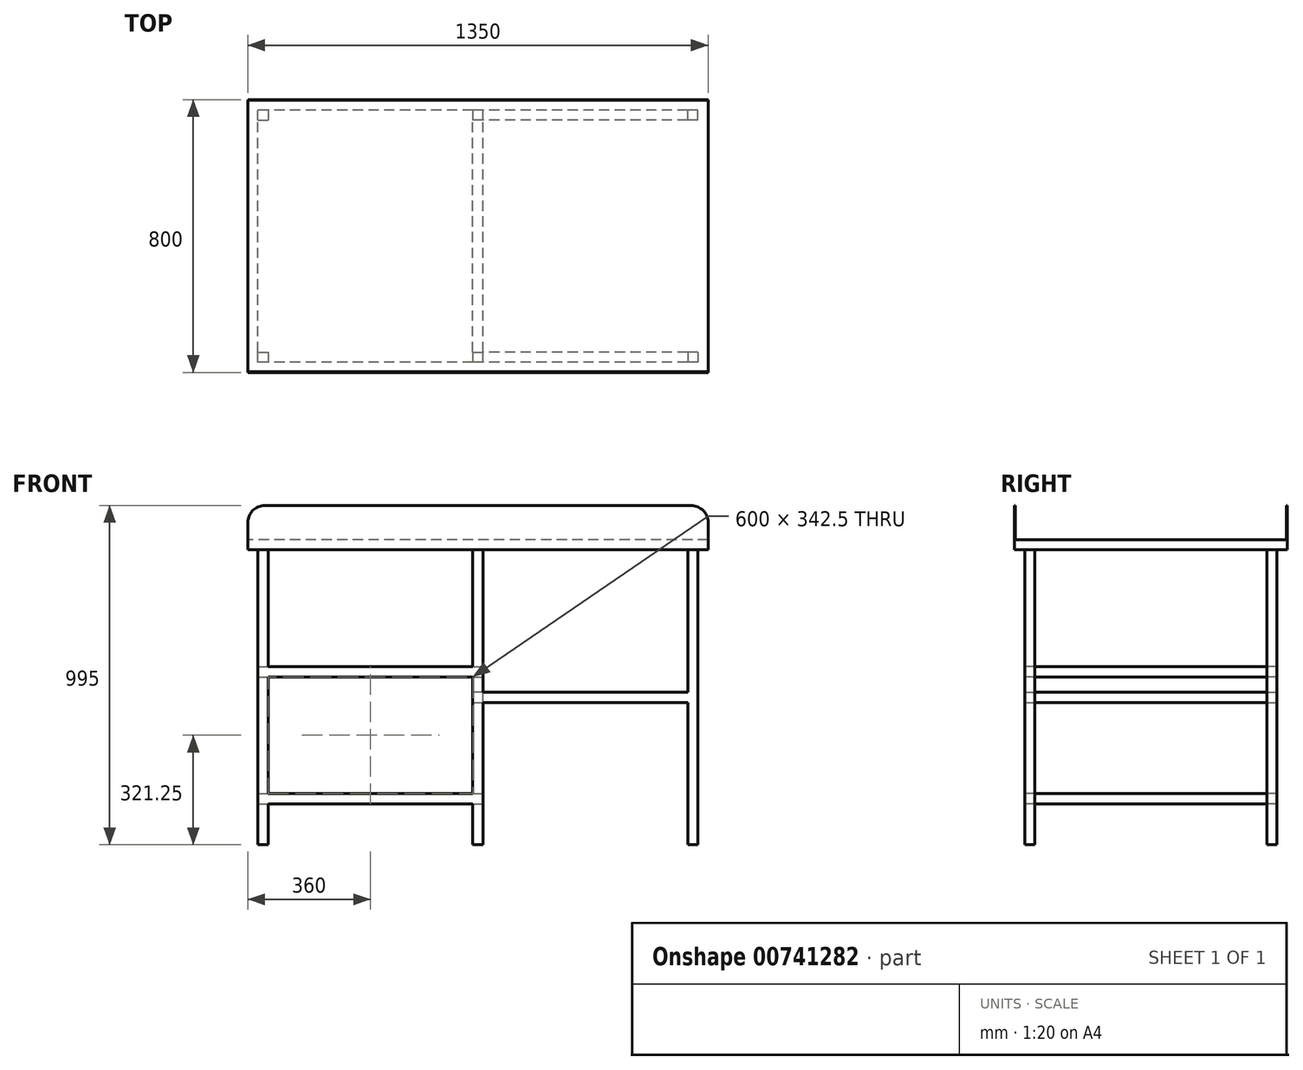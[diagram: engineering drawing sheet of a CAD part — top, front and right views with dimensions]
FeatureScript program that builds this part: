
annotation { "Feature Type Name" : "Feature", "Feature Type Description" : "" }
export const myFeature = defineFeature(function(context is Context, id is Id, definition is map)
    precondition{}
    {
        {
            var Q0;
            Q0=qCreatedBy(makeId("Right.planeOp"),FACE);
            var sketch = newSketch(context, id + "F0", { "sketchPlane" : qUnion([Q0])});
            skLineSegment(sketch, "E0", {"start": v(0, 0) * mm, "end": v(0, -130) * mm});
            skLineSegment(sketch, "E1", {"start": v(0, -130) * mm, "end": v(800, -130) * mm});
            skLineSegment(sketch, "E2", {"start": v(800, -130) * mm, "end": v(800, 0) * mm});
            skLineSegment(sketch, "E3", {"start": v(800, 0) * mm, "end": v(798, 0) * mm});
            skLineSegment(sketch, "E4", {"start": v(798, 0) * mm, "end": v(798, -100) * mm});
            skLineSegment(sketch, "E5", {"start": v(798, -100) * mm, "end": v(2, -100) * mm});
            skLineSegment(sketch, "E6", {"start": v(2, -100) * mm, "end": v(2, 0) * mm});
            skLineSegment(sketch, "E7", {"start": v(2, 0) * mm, "end": v(0, 0) * mm});
            skSolve(sketch);
        }
        {
            var Q0;
            Q0 = qSketchRegion(id + "F0", true);
            extrude(context, id + "F1", {"entities" : qUnion([Q0]), "depth" : 1350 * mm, "offsetDistance" : 25 * mm});
        }
        {
            var Q0;
            Q0=makeQuery(id+"F1.opExtrude","CAP_EDGE",EDGE,{"disambiguationData":[OSD([sQuery(id+"F0.wireOp",EDGE,"E7")])],"isStart":false});
            var Q1;
            Q1=makeQuery(id+"F1.opExtrude","CAP_EDGE",EDGE,{"disambiguationData":[OSD([sQuery(id+"F0.wireOp",EDGE,"E3")])],"isStart":false});
            var Q2;
            Q2=makeQuery(id+"F1.opExtrude","CAP_EDGE",EDGE,{"disambiguationData":[OSD([sQuery(id+"F0.wireOp",EDGE,"E3")])],"isStart":true});
            var Q3;
            Q3=makeQuery(id+"F1.opExtrude","CAP_EDGE",EDGE,{"disambiguationData":[OSD([sQuery(id+"F0.wireOp",EDGE,"E7")])],"isStart":true});
            fillet(context, id + "F2", {"entities" : qUnion([Q0, Q1, Q2, Q3]), "radius" : 50 * mm, "tangentPropagation" : true, "allowEdgeOverflow" : false});
        }
        {
            var Q0;
            Q0=makeQuery(id+"F1.opExtrude","SWEPT_FACE",FACE,{"disambiguationData":[OSD([sQuery(id+"F0.wireOp",EDGE,"E1")])]});
            var sketch = newSketch(context, id + "F3", { "sketchPlane" : qUnion([Q0])});
            skLineSegment(sketch, "E8.bottom", {"start": v(60, -30) * mm, "end": v(30, -30) * mm});
            skLineSegment(sketch, "E8.top", {"start": v(60, -60) * mm, "end": v(30, -60) * mm});
            skLineSegment(sketch, "E8.left", {"start": v(60, -30) * mm, "end": v(60, -60) * mm});
            skLineSegment(sketch, "E8.right", {"start": v(30, -30) * mm, "end": v(30, -60) * mm});
            skPoint(sketch, "E8.middle", {"position": v(45, -45) * mm});
            skLineSegment(sketch, "E9.bottom", {"start": v(1320, -60) * mm, "end": v(1290, -60) * mm});
            skLineSegment(sketch, "E9.top", {"start": v(1320, -30) * mm, "end": v(1290, -30) * mm});
            skLineSegment(sketch, "E9.left", {"start": v(1320, -60) * mm, "end": v(1320, -30) * mm});
            skLineSegment(sketch, "E9.right", {"start": v(1290, -60) * mm, "end": v(1290, -30) * mm});
            skPoint(sketch, "E9.middle", {"position": v(1305, -45) * mm});
            skLineSegment(sketch, "E10.bottom", {"start": v(1320, -740) * mm, "end": v(1290, -740) * mm});
            skLineSegment(sketch, "E10.top", {"start": v(1320, -770) * mm, "end": v(1290, -770) * mm});
            skLineSegment(sketch, "E10.left", {"start": v(1320, -740) * mm, "end": v(1320, -770) * mm});
            skLineSegment(sketch, "E10.right", {"start": v(1290, -740) * mm, "end": v(1290, -770) * mm});
            skPoint(sketch, "E10.middle", {"position": v(1305, -755) * mm});
            skLineSegment(sketch, "E11.bottom", {"start": v(60, -740) * mm, "end": v(30, -740) * mm});
            skLineSegment(sketch, "E11.top", {"start": v(60, -770) * mm, "end": v(30, -770) * mm});
            skLineSegment(sketch, "E11.left", {"start": v(60, -740) * mm, "end": v(60, -770) * mm});
            skLineSegment(sketch, "E11.right", {"start": v(30, -740) * mm, "end": v(30, -770) * mm});
            skPoint(sketch, "E11.middle", {"position": v(45, -755) * mm});
            skLineSegment(sketch, "E12.bottom", {"start": v(690, -30) * mm, "end": v(660, -30) * mm});
            skLineSegment(sketch, "E12.top", {"start": v(690, -60) * mm, "end": v(660, -60) * mm});
            skLineSegment(sketch, "E12.left", {"start": v(690, -30) * mm, "end": v(690, -60) * mm});
            skLineSegment(sketch, "E12.right", {"start": v(660, -30) * mm, "end": v(660, -60) * mm});
            skPoint(sketch, "E12.middle", {"position": v(675, -45) * mm});
            skLineSegment(sketch, "E13.bottom", {"start": v(690, -740) * mm, "end": v(660, -740) * mm});
            skLineSegment(sketch, "E13.top", {"start": v(690, -770) * mm, "end": v(660, -770) * mm});
            skLineSegment(sketch, "E13.left", {"start": v(690, -740) * mm, "end": v(690, -770) * mm});
            skLineSegment(sketch, "E13.right", {"start": v(660, -740) * mm, "end": v(660, -770) * mm});
            skPoint(sketch, "E13.middle", {"position": v(675, -755) * mm});
            skPoint(sketch, "E13.middle.positionSnap0", {"position": v(675, -60) * mm});
            skPoint(sketch, "E13.centerSnap0", {"position": v(675, -60) * mm});
            skSolve(sketch);
        }
        {
            var Q0;
            Q0 = qSketchRegion(id + "F3", true);
            extrude(context, id + "F4", {"entities" : qUnion([Q0]), "operationType" : NewBodyOperationType.ADD, "depth" : 865 * mm, "offsetDistance" : 25 * mm});
        }
        {
            var Q0;
            Q0=makeQuery(id+"F4.opExtrude","SWEPT_FACE",FACE,{"disambiguationData":[OSD([sQuery(id+"F3.wireOp",EDGE,"E8.left")])]});
            var sketch = newSketch(context, id + "F5", { "sketchPlane" : qUnion([Q0])});
            skLineSegment(sketch, "E14.bottom", {"start": v(30, -845) * mm, "end": v(770, -845) * mm});
            skLineSegment(sketch, "E14.top", {"start": v(30, -875) * mm, "end": v(770, -875) * mm});
            skLineSegment(sketch, "E14.left", {"start": v(30, -845) * mm, "end": v(30, -875) * mm});
            skLineSegment(sketch, "E14.right", {"start": v(770, -845) * mm, "end": v(770, -875) * mm});
            skLineSegment(sketch, "E15.bottom", {"start": v(30, -472.5) * mm, "end": v(770, -472.5) * mm});
            skLineSegment(sketch, "E15.top", {"start": v(30, -502.5) * mm, "end": v(770, -502.5) * mm});
            skLineSegment(sketch, "E15.left", {"start": v(30, -472.5) * mm, "end": v(30, -502.5) * mm});
            skLineSegment(sketch, "E15.right", {"start": v(770, -472.5) * mm, "end": v(770, -502.5) * mm});
            skSolve(sketch);
        }
        {
            var Q0;
            Q0 = qSketchRegion(id + "F5", true);
            var Q1;
            Q1=makeQuery(id+"F4.opExtrude","SWEPT_FACE",FACE,{"disambiguationData":[OSD([sQuery(id+"F3.wireOp",EDGE,"E12.left")])]});
            var Q2;
            Q2=makeQuery(id+"F4.opExtrude","SWEPT_FACE",FACE,{"disambiguationData":[OSD([sQuery(id+"F3.wireOp",EDGE,"E8.right")])]});
            extrude(context, id + "F6", {"entities" : qUnion([Q0]), "operationType" : NewBodyOperationType.ADD, "endBound" : BoundingType.UP_TO_SURFACE, "depth" : 25 * mm, "endBoundEntityFace" : qUnion([Q1]), "offsetDistance" : 25 * mm, "hasSecondDirection" : true, "secondDirectionBound" : SecondDirectionBoundingType.UP_TO_SURFACE, "secondDirectionOppositeDirection" : true, "secondDirectionDepth" : 25 * mm, "secondDirectionBoundEntityFace" : qUnion([Q2])});
        }
        {
            var Q0;
            {var subQ0=sQuery(id+"F3.wireOp",EDGE,"E12.left");Q0=makeQuery(id+"F6.boolean.opBoolean","MERGE",FACE,{"derivedFrom":[makeQuery(id+"F4.opExtrude","SWEPT_FACE",FACE,{"disambiguationData":[OSD([subQ0])]}),makeQuery(id+"F4.opExtrude","SWEPT_FACE",FACE,{"disambiguationData":[OSD([sQuery(id+"F3.wireOp",EDGE,"E13.left")])]}),makeQuery(id+"F6.opExtrude","CAP_FACE",FACE,{"disambiguationData":[OSD([subQ0]),OD(0.0)],"isStart":false}),makeQuery(id+"F6.opExtrude","CAP_FACE",FACE,{"disambiguationData":[OSD([subQ0]),OD(1.0)],"isStart":false})]});}
            var sketch = newSketch(context, id + "F7", { "sketchPlane" : qUnion([Q0])});
            skLineSegment(sketch, "E16.bottom", {"start": v(30, -577.5) * mm, "end": v(60, -577.5) * mm});
            skLineSegment(sketch, "E16.top", {"start": v(30, -547.5) * mm, "end": v(60, -547.5) * mm});
            skLineSegment(sketch, "E16.left", {"start": v(30, -577.5) * mm, "end": v(30, -547.5) * mm});
            skLineSegment(sketch, "E16.right", {"start": v(60, -577.5) * mm, "end": v(60, -547.5) * mm});
            skLineSegment(sketch, "E17.bottom", {"start": v(740, -547.5) * mm, "end": v(770, -547.5) * mm});
            skLineSegment(sketch, "E17.top", {"start": v(740, -577.5) * mm, "end": v(770, -577.5) * mm});
            skLineSegment(sketch, "E17.left", {"start": v(740, -547.5) * mm, "end": v(740, -577.5) * mm});
            skLineSegment(sketch, "E17.right", {"start": v(770, -547.5) * mm, "end": v(770, -577.5) * mm});
            skSolve(sketch);
        }
        {
            var Q0;
            Q0 = qSketchRegion(id + "F7", true);
            extrude(context, id + "F8", {"entities" : qUnion([Q0]), "operationType" : NewBodyOperationType.ADD, "endBound" : BoundingType.UP_TO_NEXT, "depth" : 25 * mm, "offsetDistance" : 25 * mm});
        }
        {
            var Q0;
            Q0=makeQuery(id+"F8.boolean.opBoolean","MERGE",FACE,{"derivedFrom":[makeQuery(id+"F4.opExtrude","SWEPT_FACE",FACE,{"disambiguationData":[OSD([sQuery(id+"F3.wireOp",EDGE,"E10.bottom")])]}),makeQuery(id+"F6.boolean.opBoolean","SPLIT",FACE,{"disambiguationData":[TD([makeQuery(id+"F6.opExtrude","SWEPT_FACE",FACE,{"disambiguationData":[OSD([sQuery(id+"F5.wireOp",EDGE,"E14.bottom")])]})])],"derivedFrom":makeQuery(id+"F4.opExtrude","SWEPT_FACE",FACE,{"disambiguationData":[OSD([sQuery(id+"F3.wireOp",EDGE,"E13.bottom")])]})}),makeQuery(id+"F8.opExtrude","SWEPT_FACE",FACE,{"disambiguationData":[OSD([sQuery(id+"F7.wireOp",EDGE,"E17.left")])]})]});
            var sketch = newSketch(context, id + "F9", { "sketchPlane" : qUnion([Q0])});
            skLineSegment(sketch, "E18.bottom", {"start": v(690, -547.5) * mm, "end": v(660, -547.5) * mm});
            skLineSegment(sketch, "E18.top", {"start": v(690, -577.5) * mm, "end": v(660, -577.5) * mm});
            skLineSegment(sketch, "E18.left", {"start": v(690, -547.5) * mm, "end": v(690, -577.5) * mm});
            skLineSegment(sketch, "E18.right", {"start": v(660, -547.5) * mm, "end": v(660, -577.5) * mm});
            skSolve(sketch);
        }
        {
            var Q0;
            Q0 = qSketchRegion(id + "F9", true);
            extrude(context, id + "F10", {"entities" : qUnion([Q0]), "operationType" : NewBodyOperationType.ADD, "endBound" : BoundingType.UP_TO_NEXT, "depth" : 25 * mm, "offsetDistance" : 25 * mm});
        }
    });
